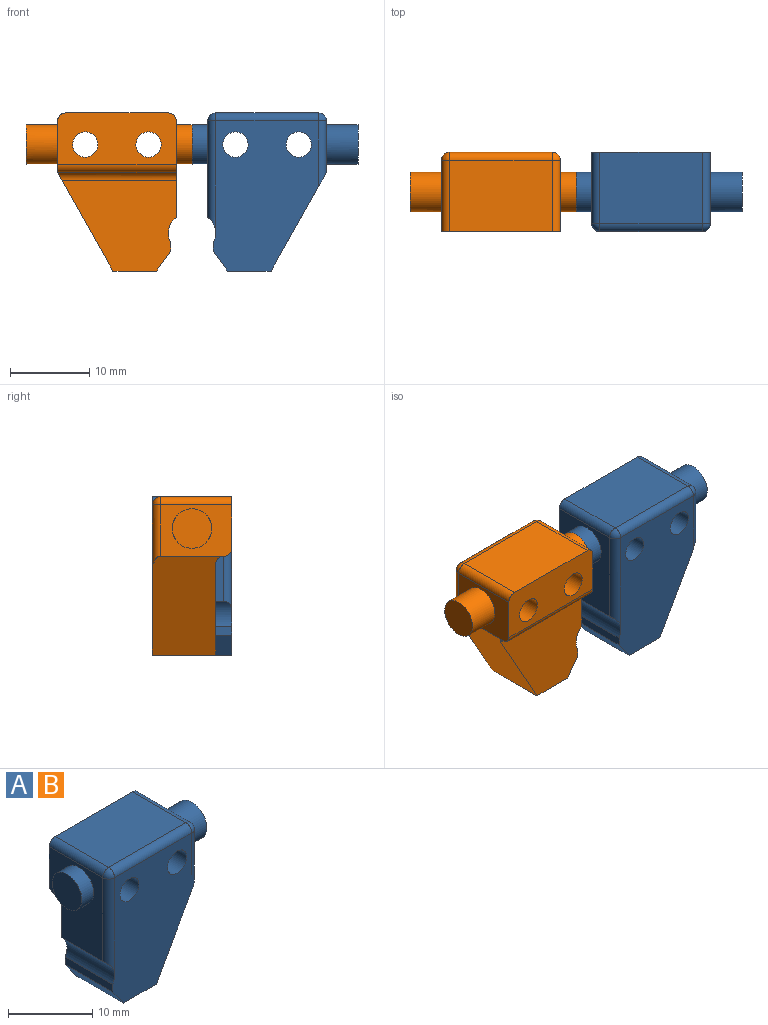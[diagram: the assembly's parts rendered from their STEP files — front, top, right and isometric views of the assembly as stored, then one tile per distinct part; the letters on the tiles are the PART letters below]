
ASSEMBLY  parts=2 mates=1
PART A: 26 faces, bbox 21x10x20 mm
  f0: plane 12.2x9mm, normal (-1,0,0), area 78.8mm2, adj f1,f5,f12,f13,f14,f19,f21,f22
  f1: cylinder r=2.5mm len=8mm, axis (0,1,0), area 28.1mm2, adj f0,f2,f11,f12,f19
  f2: plane 8x1.11mm, normal (-1,0,0), area 8.9mm2, adj f1,f3,f11,f12
  f3: plane 8x2.5mm, normal (-0.81,0,-0.58), area 24.6mm2, adj f2,f7,f11,f12
  f4: plane 12.5x9mm, normal (0.87,0,-0.49), area 114.4mm2, adj f7,f9,f11,f12,f14,f16
  f5: plane 15x6.5mm, normal (0,1,0), area 81mm2, adj f0,f6,f8,f9,f10,f13,f15,f21
  f6: plane 13x9mm, normal (0,0,1), area 117mm2, adj f5,f15,f18,f21
  f7: plane 8x5.5mm, normal (0,0,-1), area 44mm2, adj f3,f4,f11,f12
  f8: cylinder r=1.6mm len=10mm, axis (0,1,0), area 100.5mm2, adj f5,f11
  f9: plane 9x6.5mm, normal (1,0,0), area 38.7mm2, adj f4,f5,f13,f15,f16,f24
  f10: cylinder r=1.6mm len=10mm, axis (0,1,0), area 100.5mm2, adj f5,f11
  f11: plane 19x13.3mm, normal (0,-1,0), area 197.7mm2, adj f1,f2,f3,f4,f7,f8,f10,f16
  f12: plane 14.44x11.5mm, normal (0,1,0), area 121.8mm2, adj f0,f1,f2,f3,f4,f7,f14
  f13: cylinder r=1mm len=15mm, axis (-1,0,0), area 23.6mm2, adj f0,f5,f9,f14
  f14: cylinder r=1mm len=15mm, axis (-1,0,0), area 23.2mm2, adj f0,f4,f12,f13
  f15: cylinder r=1mm len=9mm, axis (0,-1,0), area 14.1mm2, adj f5,f6,f9,f17
  f16: cylinder r=1mm len=8.29mm, axis (0,0,-1), area 11.2mm2, adj f4,f9,f11,f17
  f17: sphere r=1mm, area 1.6mm2, adj f15,f16,f18
  f18: cylinder r=1mm len=13mm, axis (1,0,0), area 20.4mm2, adj f6,f11,f17,f20
  f19: cylinder r=1mm len=14.2mm, axis (0,0,1), area 19.8mm2, adj f0,f1,f11,f20
  f20: sphere r=1mm, area 1.6mm2, adj f18,f19,f21
  f21: cylinder r=1mm len=9mm, axis (0,1,0), area 14.1mm2, adj f0,f5,f6,f20
  f22: cylinder r=2.5mm len=5mm, axis (1,0,0), area 31.4mm2, adj f0,f23
  f23: plane 5x5mm, normal (-1,0,0), area 19.6mm2, adj f22
  f24: cylinder r=2.5mm len=5mm, axis (-1,0,0), area 62.8mm2, adj f9,f25
  f25: plane 5x5mm, normal (1,0,0), area 19.6mm2, adj f24
PART B: same geometry as A
PLACE A t=(34.68,10.27,-9.73)mm
PLACE B rot(axis=(0,0,1),180deg) t=(15.68,10.27,-9.73)mm
MATE fastened B.f22 <-> A.f22  axis (1,0,0) through (25.18,10.27,-9.73)mm
